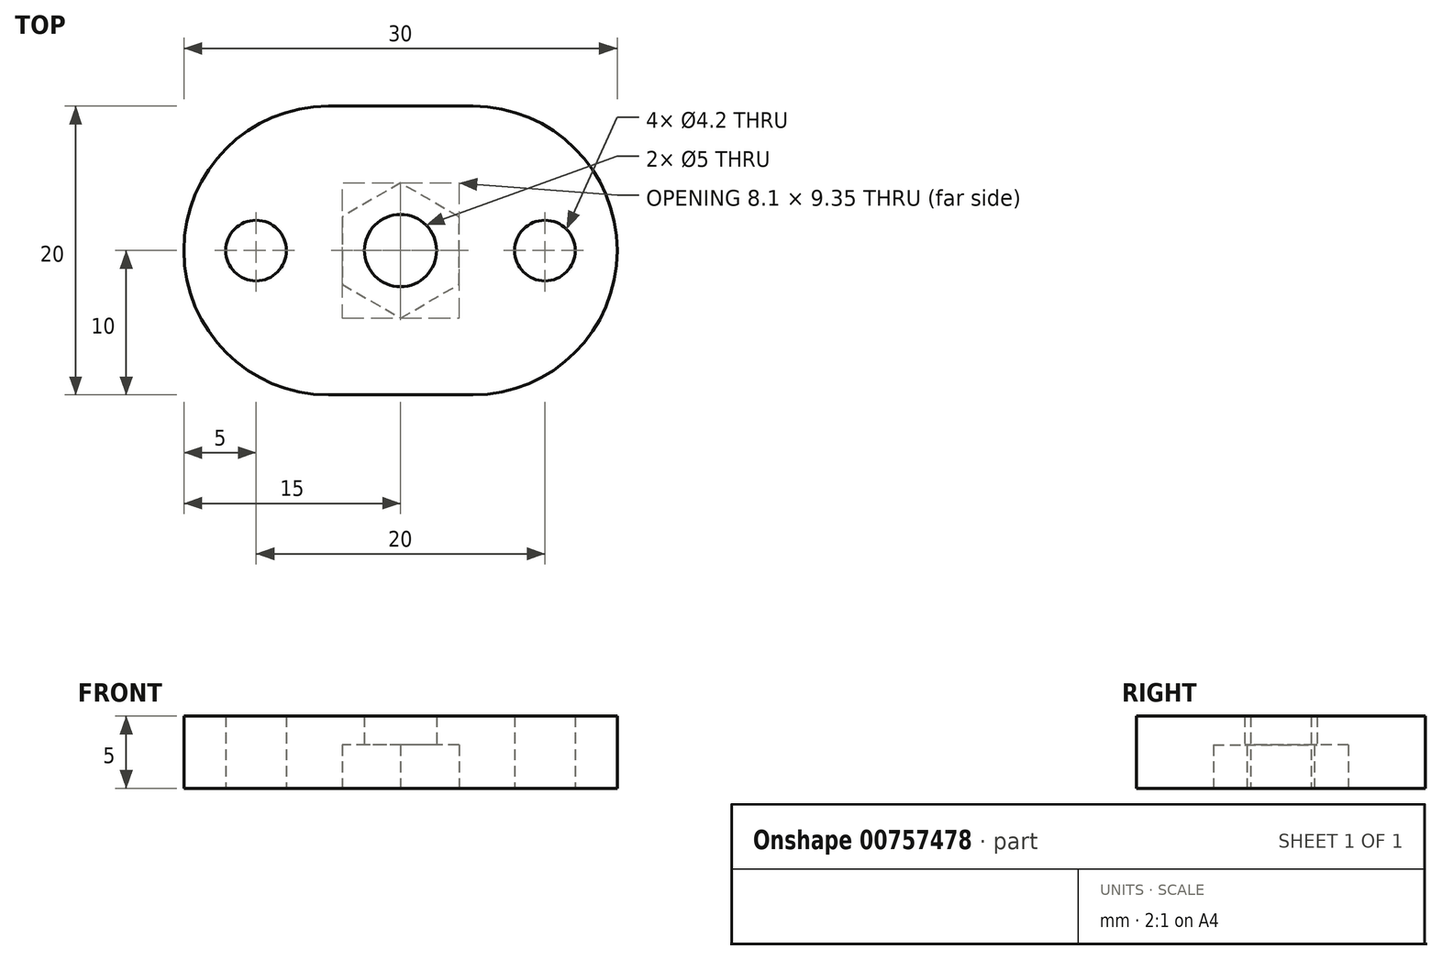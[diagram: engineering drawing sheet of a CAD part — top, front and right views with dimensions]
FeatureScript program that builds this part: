
annotation { "Feature Type Name" : "Feature", "Feature Type Description" : "" }
export const myFeature = defineFeature(function(context is Context, id is Id, definition is map)
    precondition{}
    {
        {
            var Q0;
            Q0=qCreatedBy(makeId("Top.planeOp"),FACE);
            var sketch = newSketch(context, id + "F0", { "sketchPlane" : qUnion([Q0])});
            skLineSegment(sketch, "E0", {"start": v(0, 0) * mm, "end": v(0, -20) * mm, "construction": true});
            skCircle(sketch, "E1", {"center": v(0, -10) * mm, "radius": 2.1 * mm});
            skLineSegment(sketch, "E2", {"start": v(-20, 0) * mm, "end": v(-20, -20) * mm, "construction": true});
            skCircle(sketch, "E3", {"center": v(-20, -10) * mm, "radius": 2.1 * mm});
            skLineSegment(sketch, "E4", {"start": v(-20, 0) * mm, "end": v(0, 0) * mm});
            skLineSegment(sketch, "E5", {"start": v(-20, -20) * mm, "end": v(0, -20) * mm});
            skLineSegment(sketch, "E6", {"start": v(-10, 0) * mm, "end": v(-10, -20) * mm, "construction": true});
            skCircle(sketch, "E7", {"center": v(-10, -10) * mm, "radius": 2.5 * mm});
            skLineSegment(sketch, "E8", {"start": v(-20, 0) * mm, "end": v(-25, 0) * mm});
            skLineSegment(sketch, "E9", {"start": v(-25, 0) * mm, "end": v(-25, -20) * mm});
            skLineSegment(sketch, "E10", {"start": v(-25, -20) * mm, "end": v(-20, -20) * mm});
            skLineSegment(sketch, "E11", {"start": v(0, 0) * mm, "end": v(5, 0) * mm});
            skLineSegment(sketch, "E12", {"start": v(5, 0) * mm, "end": v(5, -20) * mm});
            skLineSegment(sketch, "E13", {"start": v(5, -20) * mm, "end": v(0, -20) * mm});
            skSolve(sketch);
        }
        {
            var Q0;
            Q0=makeQuery(id+"F0.imprint","IMPRINT",FACE,{"disambiguationData":[TD([[makeQuery(id+"F0.imprint","IMPRINT",EDGE,{"derivedFrom":sQuery(id+"F0.wireOp",EDGE,"E1")}),-1.0]])]});
            extrude(context, id + "F1", {"entities" : qUnion([Q0]), "depth" : 5 * mm, "offsetDistance" : 25 * mm});
        }
        {
            var Q0;
            Q0=makeQuery(id+"F1.opExtrude","SWEPT_EDGE",EDGE,{"disambiguationData":[OSD([sQuery(id+"F0.wireOp",EDGE,"E9"),sQuery(id+"F0.wireOp",EDGE,"E10")])]});
            var Q1;
            Q1=makeQuery(id+"F1.opExtrude","SWEPT_EDGE",EDGE,{"disambiguationData":[OSD([sQuery(id+"F0.wireOp",EDGE,"E12"),sQuery(id+"F0.wireOp",EDGE,"E13")])]});
            var Q2;
            Q2=makeQuery(id+"F1.opExtrude","SWEPT_EDGE",EDGE,{"disambiguationData":[OSD([sQuery(id+"F0.wireOp",EDGE,"E11"),sQuery(id+"F0.wireOp",EDGE,"E12")])]});
            var Q3;
            Q3=makeQuery(id+"F1.opExtrude","SWEPT_EDGE",EDGE,{"disambiguationData":[OSD([sQuery(id+"F0.wireOp",EDGE,"E8"),sQuery(id+"F0.wireOp",EDGE,"E9")])]});
            fillet(context, id + "F2", {"entities" : qUnion([Q0, Q1, Q2, Q3]), "radius" : 10 * mm, "tangentPropagation" : true, "allowEdgeOverflow" : false});
        }
        {
            var Q0;
            Q0=makeQuery(id+"F1.opExtrude","CAP_FACE",FACE,{"disambiguationData":[OSD([sQuery(id+"F0.wireOp",EDGE,"E1"),sQuery(id+"F0.wireOp",EDGE,"E3"),sQuery(id+"F0.wireOp",EDGE,"E4"),sQuery(id+"F0.wireOp",EDGE,"E5"),sQuery(id+"F0.wireOp",EDGE,"E7"),sQuery(id+"F0.wireOp",EDGE,"E8"),sQuery(id+"F0.wireOp",EDGE,"E9"),sQuery(id+"F0.wireOp",EDGE,"E10"),sQuery(id+"F0.wireOp",EDGE,"E11"),sQuery(id+"F0.wireOp",EDGE,"E12"),sQuery(id+"F0.wireOp",EDGE,"E13")])],"isStart":true});
            var sketch = newSketch(context, id + "F3", { "sketchPlane" : qUnion([Q0])});
            skCircle(sketch, "E14.0", {"center": v(-10, 10) * mm, "radius": 2.5 * mm});
            skCircle(sketch, "E15.cCircle", {"center": v(-10, 10) * mm, "radius": 4.05 * mm, "construction": true});
            skLineSegment(sketch, "E15.0", {"start": v(-14.05, 7.66) * mm, "end": v(-14.05, 12.34) * mm});
            skLineSegment(sketch, "E15.1", {"start": v(-14.05, 12.34) * mm, "end": v(-10, 14.68) * mm});
            skLineSegment(sketch, "E15.2", {"start": v(-10, 14.68) * mm, "end": v(-5.95, 12.34) * mm});
            skLineSegment(sketch, "E15.3", {"start": v(-5.95, 12.34) * mm, "end": v(-5.95, 7.66) * mm});
            skLineSegment(sketch, "E15.4", {"start": v(-5.95, 7.66) * mm, "end": v(-10, 5.32) * mm});
            skLineSegment(sketch, "E15.5", {"start": v(-10, 5.32) * mm, "end": v(-14.05, 7.66) * mm});
            skPoint(sketch, "E15.0.midPoint", {"position": v(-14.05, 10) * mm});
            skSolve(sketch);
        }
        {
            var Q0;
            Q0=makeQuery(id+"F3.imprint","IMPRINT",FACE,{"disambiguationData":[TD([[makeQuery(id+"F3.imprint","IMPRINT",EDGE,{"derivedFrom":sQuery(id+"F3.wireOp",EDGE,"E14.0")}),1.0]])]});
            extrude(context, id + "F4", {"entities" : qUnion([Q0]), "operationType" : NewBodyOperationType.REMOVE, "oppositeDirection" : true, "depth" : 3 * mm, "offsetDistance" : 25 * mm});
        }
    });
